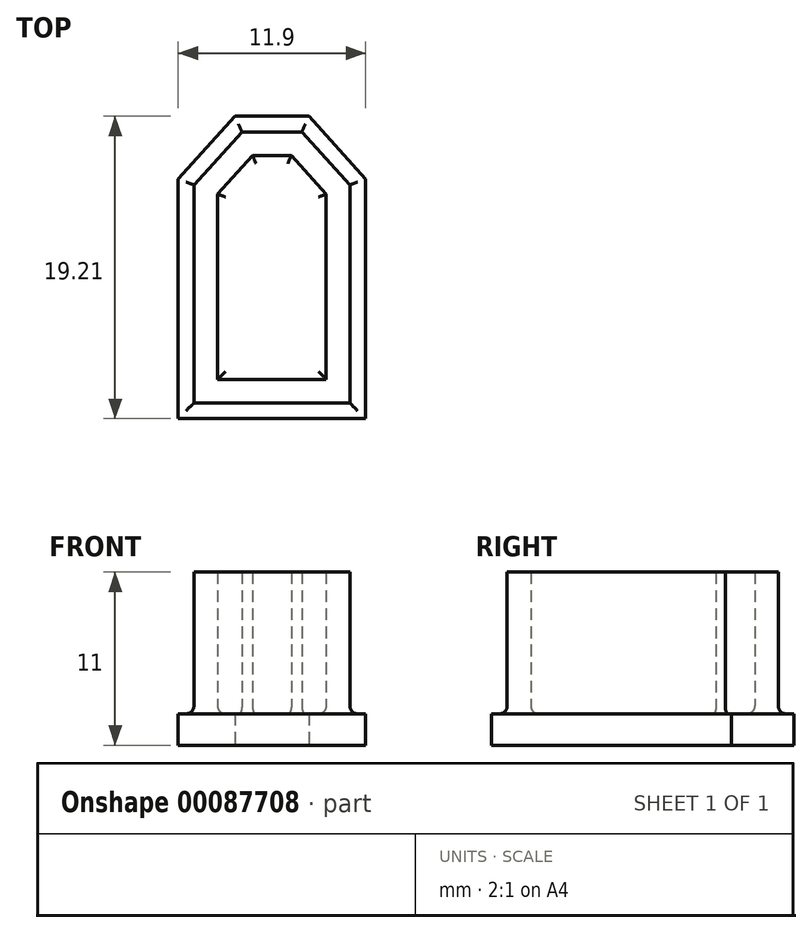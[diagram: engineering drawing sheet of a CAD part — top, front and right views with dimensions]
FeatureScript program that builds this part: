
annotation { "Feature Type Name" : "Feature", "Feature Type Description" : "" }
export const myFeature = defineFeature(function(context is Context, id is Id, definition is map)
    precondition{}
    {
        {
            var Q0;
            Q0=qCreatedBy(makeId("Top.planeOp"),FACE);
            var sketch = newSketch(context, id + "F0", { "sketchPlane" : qUnion([Q0])});
            skLineSegment(sketch, "E0.bottom", {"start": v(3.45, 5.88) * mm, "end": v(-3.45, 5.89) * mm});
            skLineSegment(sketch, "E0.top", {"start": v(3.45, -5.89) * mm, "end": v(-3.45, -5.88) * mm});
            skLineSegment(sketch, "E0.left", {"start": v(3.45, 5.88) * mm, "end": v(3.45, -5.89) * mm});
            skLineSegment(sketch, "E0.right", {"start": v(-3.45, 5.89) * mm, "end": v(-3.45, -5.88) * mm});
            skPoint(sketch, "E0.middle", {"position": v(0, 0) * mm});
            skLineSegment(sketch, "E1", {"start": v(-3.45, 5.89) * mm, "end": v(-1.24, 8.33) * mm});
            skLineSegment(sketch, "E2", {"start": v(-1.24, 8.33) * mm, "end": v(1.24, 8.33) * mm});
            skLineSegment(sketch, "E3", {"start": v(1.24, 8.33) * mm, "end": v(3.45, 5.88) * mm});
            skLineSegment(sketch, "E4.0", {"start": v(-4.95, 6.46) * mm, "end": v(-4.95, -7.38) * mm});
            skLineSegment(sketch, "E4.1", {"start": v(-1.9, 9.83) * mm, "end": v(1.9, 9.83) * mm});
            skLineSegment(sketch, "E4.2", {"start": v(1.9, 9.83) * mm, "end": v(4.95, 6.46) * mm});
            skLineSegment(sketch, "E4.3", {"start": v(-4.95, 6.46) * mm, "end": v(-1.9, 9.83) * mm});
            skLineSegment(sketch, "E4.4", {"start": v(4.95, 6.46) * mm, "end": v(4.95, -7.39) * mm});
            skLineSegment(sketch, "E4.5", {"start": v(4.95, -7.39) * mm, "end": v(-4.95, -7.38) * mm});
            skLineSegment(sketch, "E5.0", {"start": v(-5.95, 6.85) * mm, "end": v(-2.35, 10.83) * mm});
            skLineSegment(sketch, "E5.1", {"start": v(5.95, -8.39) * mm, "end": v(-5.95, -8.38) * mm});
            skLineSegment(sketch, "E5.2", {"start": v(5.95, 6.85) * mm, "end": v(5.95, -8.39) * mm});
            skLineSegment(sketch, "E5.3", {"start": v(-5.95, 6.85) * mm, "end": v(-5.95, -8.38) * mm});
            skLineSegment(sketch, "E5.4", {"start": v(2.35, 10.83) * mm, "end": v(5.95, 6.85) * mm});
            skLineSegment(sketch, "E5.5", {"start": v(-2.35, 10.83) * mm, "end": v(2.35, 10.83) * mm});
            skSolve(sketch);
        }
        {
            var Q0;
            Q0 = qSketchRegion(id + "F0", true);
            var Q1;
            Q1=makeQuery(id+"F0.imprint","IMPRINT",FACE,{"disambiguationData":[TD([[makeQuery(id+"F0.imprint","IMPRINT",EDGE,{"derivedFrom":sQuery(id+"F0.wireOp",EDGE,"E0.top")}),1.0]])]});
            var Q2;
            Q2=makeQuery(id+"F0.imprint","IMPRINT",FACE,{"disambiguationData":[TD([[makeQuery(id+"F0.imprint","IMPRINT",EDGE,{"derivedFrom":sQuery(id+"F0.wireOp",EDGE,"E0.bottom")}),-1.0]])]});
            var Q3;
            Q3=makeQuery(id+"F0.imprint","IMPRINT",FACE,{"disambiguationData":[TD([[makeQuery(id+"F0.imprint","IMPRINT",EDGE,{"derivedFrom":sQuery(id+"F0.wireOp",EDGE,"E0.bottom")}),1.0]])]});
            extrude(context, id + "F1", {"entities" : qUnion([Q0, Q1, Q2, Q3]), "depth" : 2 * mm});
        }
        {
            var Q0;
            Q0=makeQuery(id+"F0.imprint","IMPRINT",FACE,{"disambiguationData":[TD([[makeQuery(id+"F0.imprint","IMPRINT",EDGE,{"derivedFrom":sQuery(id+"F0.wireOp",EDGE,"E0.top")}),1.0]])]});
            extrude(context, id + "F2", {"entities" : qUnion([Q0]), "operationType" : NewBodyOperationType.ADD, "depth" : 11 * mm});
        }
        {
            var Q0;
            Q0=makeQuery(id+"F2.boolean.opBoolean","INTERSECT",EDGE,{"derivedFrom":[makeQuery(id+"F1.opExtrude","CAP_FACE",FACE,{"disambiguationData":[OSD([sQuery(id+"F0.wireOp",EDGE,"E5.0"),sQuery(id+"F0.wireOp",EDGE,"E5.1"),sQuery(id+"F0.wireOp",EDGE,"E5.2"),sQuery(id+"F0.wireOp",EDGE,"E5.3"),sQuery(id+"F0.wireOp",EDGE,"E5.4"),sQuery(id+"F0.wireOp",EDGE,"E5.5")])],"isStart":false}),makeQuery(id+"F2.opExtrude","SWEPT_FACE",FACE,{"disambiguationData":[OSD([sQuery(id+"F0.wireOp",EDGE,"E0.right")])]})]});
            var Q1;
            Q1=makeQuery(id+"F2.boolean.opBoolean","INTERSECT",EDGE,{"derivedFrom":[makeQuery(id+"F1.opExtrude","CAP_FACE",FACE,{"disambiguationData":[OSD([sQuery(id+"F0.wireOp",EDGE,"E5.0"),sQuery(id+"F0.wireOp",EDGE,"E5.1"),sQuery(id+"F0.wireOp",EDGE,"E5.2"),sQuery(id+"F0.wireOp",EDGE,"E5.3"),sQuery(id+"F0.wireOp",EDGE,"E5.4"),sQuery(id+"F0.wireOp",EDGE,"E5.5")])],"isStart":false}),makeQuery(id+"F2.opExtrude","SWEPT_FACE",FACE,{"disambiguationData":[OSD([sQuery(id+"F0.wireOp",EDGE,"E1")])]})]});
            var Q2;
            Q2=makeQuery(id+"F2.boolean.opBoolean","INTERSECT",EDGE,{"derivedFrom":[makeQuery(id+"F1.opExtrude","CAP_FACE",FACE,{"disambiguationData":[OSD([sQuery(id+"F0.wireOp",EDGE,"E5.0"),sQuery(id+"F0.wireOp",EDGE,"E5.1"),sQuery(id+"F0.wireOp",EDGE,"E5.2"),sQuery(id+"F0.wireOp",EDGE,"E5.3"),sQuery(id+"F0.wireOp",EDGE,"E5.4"),sQuery(id+"F0.wireOp",EDGE,"E5.5")])],"isStart":false}),makeQuery(id+"F2.opExtrude","SWEPT_FACE",FACE,{"disambiguationData":[OSD([sQuery(id+"F0.wireOp",EDGE,"E2")])]})]});
            var Q3;
            Q3=makeQuery(id+"F2.boolean.opBoolean","INTERSECT",EDGE,{"derivedFrom":[makeQuery(id+"F1.opExtrude","CAP_FACE",FACE,{"disambiguationData":[OSD([sQuery(id+"F0.wireOp",EDGE,"E5.0"),sQuery(id+"F0.wireOp",EDGE,"E5.1"),sQuery(id+"F0.wireOp",EDGE,"E5.2"),sQuery(id+"F0.wireOp",EDGE,"E5.3"),sQuery(id+"F0.wireOp",EDGE,"E5.4"),sQuery(id+"F0.wireOp",EDGE,"E5.5")])],"isStart":false}),makeQuery(id+"F2.opExtrude","SWEPT_FACE",FACE,{"disambiguationData":[OSD([sQuery(id+"F0.wireOp",EDGE,"E3")])]})]});
            var Q4;
            Q4=makeQuery(id+"F2.boolean.opBoolean","INTERSECT",EDGE,{"derivedFrom":[makeQuery(id+"F1.opExtrude","CAP_FACE",FACE,{"disambiguationData":[OSD([sQuery(id+"F0.wireOp",EDGE,"E5.0"),sQuery(id+"F0.wireOp",EDGE,"E5.1"),sQuery(id+"F0.wireOp",EDGE,"E5.2"),sQuery(id+"F0.wireOp",EDGE,"E5.3"),sQuery(id+"F0.wireOp",EDGE,"E5.4"),sQuery(id+"F0.wireOp",EDGE,"E5.5")])],"isStart":false}),makeQuery(id+"F2.opExtrude","SWEPT_FACE",FACE,{"disambiguationData":[OSD([sQuery(id+"F0.wireOp",EDGE,"E0.left")])]})]});
            var Q5;
            Q5=makeQuery(id+"F2.boolean.opBoolean","INTERSECT",EDGE,{"derivedFrom":[makeQuery(id+"F1.opExtrude","CAP_FACE",FACE,{"disambiguationData":[OSD([sQuery(id+"F0.wireOp",EDGE,"E5.0"),sQuery(id+"F0.wireOp",EDGE,"E5.1"),sQuery(id+"F0.wireOp",EDGE,"E5.2"),sQuery(id+"F0.wireOp",EDGE,"E5.3"),sQuery(id+"F0.wireOp",EDGE,"E5.4"),sQuery(id+"F0.wireOp",EDGE,"E5.5")])],"isStart":false}),makeQuery(id+"F2.opExtrude","SWEPT_FACE",FACE,{"disambiguationData":[OSD([sQuery(id+"F0.wireOp",EDGE,"E0.top")])]})]});
            var Q6;
            Q6=makeQuery(id+"F2.boolean.opBoolean","INTERSECT",EDGE,{"derivedFrom":[makeQuery(id+"F1.opExtrude","CAP_FACE",FACE,{"disambiguationData":[OSD([sQuery(id+"F0.wireOp",EDGE,"E5.0"),sQuery(id+"F0.wireOp",EDGE,"E5.1"),sQuery(id+"F0.wireOp",EDGE,"E5.2"),sQuery(id+"F0.wireOp",EDGE,"E5.3"),sQuery(id+"F0.wireOp",EDGE,"E5.4"),sQuery(id+"F0.wireOp",EDGE,"E5.5")])],"isStart":false}),makeQuery(id+"F2.opExtrude","SWEPT_FACE",FACE,{"disambiguationData":[OSD([sQuery(id+"F0.wireOp",EDGE,"E4.5")])]})]});
            var Q7;
            Q7=makeQuery(id+"F2.boolean.opBoolean","INTERSECT",EDGE,{"derivedFrom":[makeQuery(id+"F1.opExtrude","CAP_FACE",FACE,{"disambiguationData":[OSD([sQuery(id+"F0.wireOp",EDGE,"E5.0"),sQuery(id+"F0.wireOp",EDGE,"E5.1"),sQuery(id+"F0.wireOp",EDGE,"E5.2"),sQuery(id+"F0.wireOp",EDGE,"E5.3"),sQuery(id+"F0.wireOp",EDGE,"E5.4"),sQuery(id+"F0.wireOp",EDGE,"E5.5")])],"isStart":false}),makeQuery(id+"F2.opExtrude","SWEPT_FACE",FACE,{"disambiguationData":[OSD([sQuery(id+"F0.wireOp",EDGE,"E4.4")])]})]});
            var Q8;
            Q8=makeQuery(id+"F2.boolean.opBoolean","INTERSECT",EDGE,{"derivedFrom":[makeQuery(id+"F1.opExtrude","CAP_FACE",FACE,{"disambiguationData":[OSD([sQuery(id+"F0.wireOp",EDGE,"E5.0"),sQuery(id+"F0.wireOp",EDGE,"E5.1"),sQuery(id+"F0.wireOp",EDGE,"E5.2"),sQuery(id+"F0.wireOp",EDGE,"E5.3"),sQuery(id+"F0.wireOp",EDGE,"E5.4"),sQuery(id+"F0.wireOp",EDGE,"E5.5")])],"isStart":false}),makeQuery(id+"F2.opExtrude","SWEPT_FACE",FACE,{"disambiguationData":[OSD([sQuery(id+"F0.wireOp",EDGE,"E4.2")])]})]});
            var Q9;
            Q9=makeQuery(id+"F2.boolean.opBoolean","INTERSECT",EDGE,{"derivedFrom":[makeQuery(id+"F1.opExtrude","CAP_FACE",FACE,{"disambiguationData":[OSD([sQuery(id+"F0.wireOp",EDGE,"E5.0"),sQuery(id+"F0.wireOp",EDGE,"E5.1"),sQuery(id+"F0.wireOp",EDGE,"E5.2"),sQuery(id+"F0.wireOp",EDGE,"E5.3"),sQuery(id+"F0.wireOp",EDGE,"E5.4"),sQuery(id+"F0.wireOp",EDGE,"E5.5")])],"isStart":false}),makeQuery(id+"F2.opExtrude","SWEPT_FACE",FACE,{"disambiguationData":[OSD([sQuery(id+"F0.wireOp",EDGE,"E4.1")])]})]});
            var Q10;
            Q10=makeQuery(id+"F2.boolean.opBoolean","INTERSECT",EDGE,{"derivedFrom":[makeQuery(id+"F1.opExtrude","CAP_FACE",FACE,{"disambiguationData":[OSD([sQuery(id+"F0.wireOp",EDGE,"E5.0"),sQuery(id+"F0.wireOp",EDGE,"E5.1"),sQuery(id+"F0.wireOp",EDGE,"E5.2"),sQuery(id+"F0.wireOp",EDGE,"E5.3"),sQuery(id+"F0.wireOp",EDGE,"E5.4"),sQuery(id+"F0.wireOp",EDGE,"E5.5")])],"isStart":false}),makeQuery(id+"F2.opExtrude","SWEPT_FACE",FACE,{"disambiguationData":[OSD([sQuery(id+"F0.wireOp",EDGE,"E4.3")])]})]});
            var Q11;
            Q11=makeQuery(id+"F2.boolean.opBoolean","INTERSECT",EDGE,{"derivedFrom":[makeQuery(id+"F1.opExtrude","CAP_FACE",FACE,{"disambiguationData":[OSD([sQuery(id+"F0.wireOp",EDGE,"E5.0"),sQuery(id+"F0.wireOp",EDGE,"E5.1"),sQuery(id+"F0.wireOp",EDGE,"E5.2"),sQuery(id+"F0.wireOp",EDGE,"E5.3"),sQuery(id+"F0.wireOp",EDGE,"E5.4"),sQuery(id+"F0.wireOp",EDGE,"E5.5")])],"isStart":false}),makeQuery(id+"F2.opExtrude","SWEPT_FACE",FACE,{"disambiguationData":[OSD([sQuery(id+"F0.wireOp",EDGE,"E4.0")])]})]});
            fillet(context, id + "F3", {"entities" : qUnion([Q0, Q1, Q2, Q3, Q4, Q5, Q6, Q7, Q8, Q9, Q10, Q11]), "radius" : .5 * mm, "tangentPropagation" : true, "allowEdgeOverflow" : false});
        }
    });
